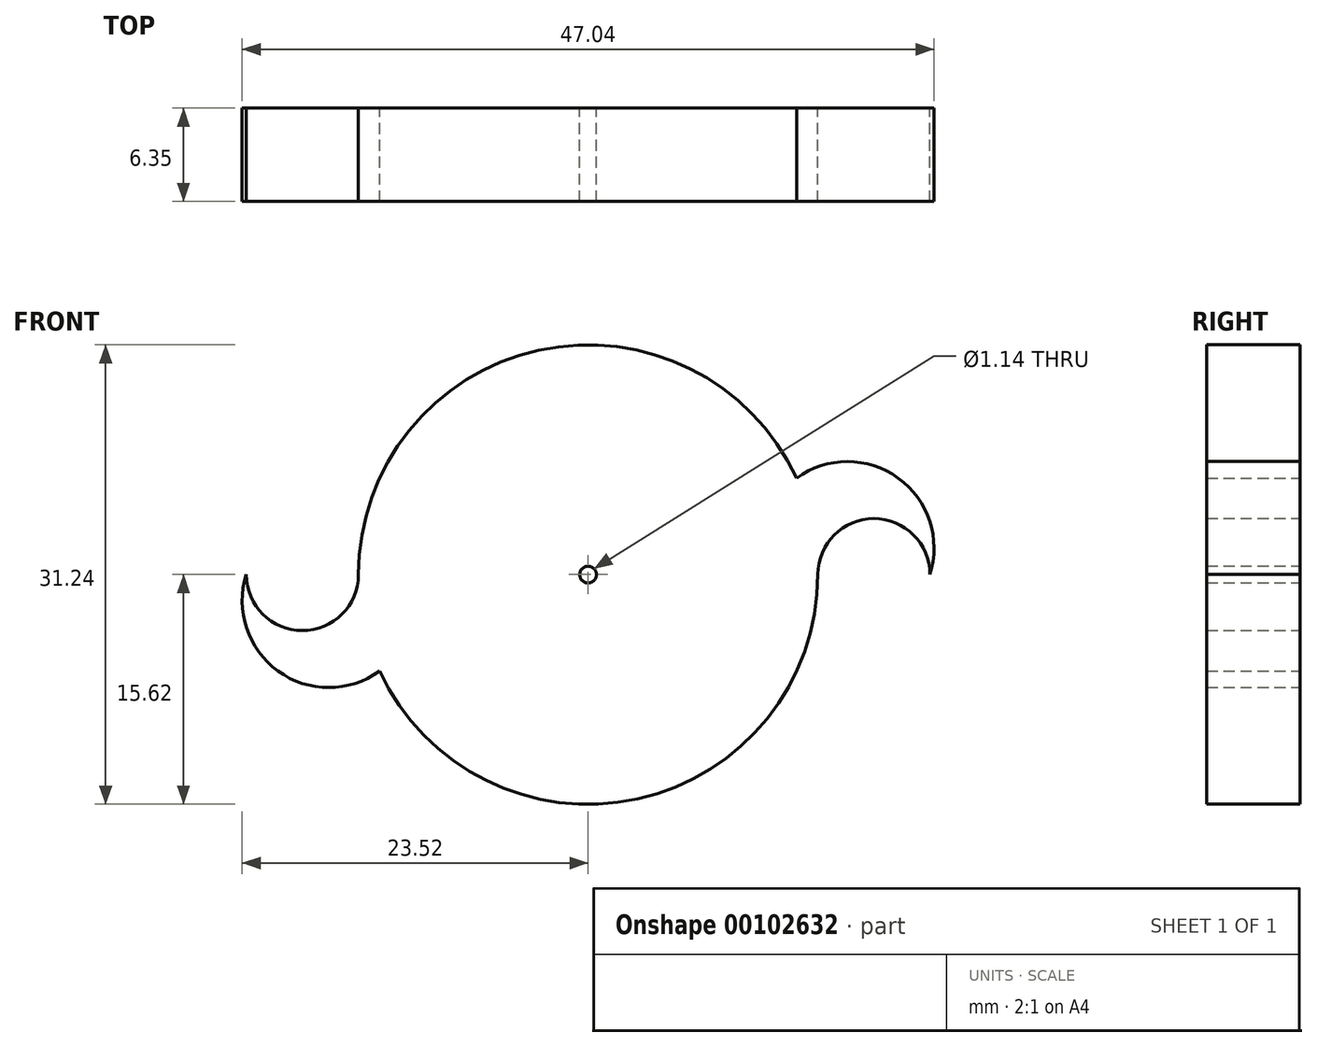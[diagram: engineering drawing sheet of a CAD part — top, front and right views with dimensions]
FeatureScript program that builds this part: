
annotation { "Feature Type Name" : "Feature", "Feature Type Description" : "" }
export const myFeature = defineFeature(function(context is Context, id is Id, definition is map)
    precondition{}
    {
        {
            var Q0;
            Q0=qCreatedBy(makeId("Front.planeOp"),FACE);
            var sketch = newSketch(context, id + "F0", { "sketchPlane" : qUnion([Q0])});
            skArc(sketch, "E0", {"start": v(14.18, 6.56) * mm, "mid": v(-3.36, 15.26) * mm, "end": v(-15.62, 0) * mm});
            skLineSegment(sketch, "E1", {"start": v(31, -8.23) * mm, "end": v(46.62, -8.23) * mm, "construction": true});
            skLineSegment(sketch, "E2", {"start": v(46.62, -8.23) * mm, "end": v(54.24, -8.23) * mm, "construction": true});
            skLineSegment(sketch, "E3", {"start": v(0, 0) * mm, "end": v(15.62, 0) * mm, "construction": true});
            skArc(sketch, "E4", {"start": v(15.62, 0) * mm, "mid": v(19.43, 3.81) * mm, "end": v(23.24, 0) * mm});
            skLineSegment(sketch, "E5", {"start": v(15.62, 0) * mm, "end": v(23.24, 0) * mm, "construction": true});
            skCircle(sketch, "E6", {"center": v(0, 0) * mm, "radius": 0.57 * mm});
            skArc(sketch, "E7", {"start": v(23.24, 0) * mm, "mid": v(21.09, 6.56) * mm, "end": v(14.18, 6.56) * mm});
            skLineSegment(sketch, "E8", {"start": v(17.63, 1.8) * mm, "end": v(19.43, 0) * mm, "construction": true});
            skArc(sketch, "E9.1.0", {"start": v(-23.24, 0) * mm, "mid": v(-21.09, -6.56) * mm, "end": v(-14.18, -6.56) * mm});
            skArc(sketch, "E9.1.1", {"start": v(-15.62, 0) * mm, "mid": v(-19.43, -3.81) * mm, "end": v(-23.24, 0) * mm});
            skArc(sketch, "E10.trimOffspring", {"start": v(-12.14, -9.83) * mm, "mid": v(5.21, -14.73) * mm, "end": v(15.62, 0) * mm});
            skArc(sketch, "E11.trimOffspring", {"start": v(-14.18, -6.56) * mm, "mid": v(-14, -6.92) * mm, "end": v(-13.82, -7.28) * mm});
            skArc(sketch, "E12.trimOffspring", {"start": v(-1.4, -15.56) * mm, "mid": v(10.54, -11.53) * mm, "end": v(15.62, 0) * mm});
            skArc(sketch, "E13.trimOffspring", {"start": v(-14.18, -6.56) * mm, "mid": v(3.36, -15.26) * mm, "end": v(15.62, 0) * mm});
            skSolve(sketch);
        }
        {
            var Q0;
            Q0=qSketchRegion(id+"F0",true);
            extrude(context, id + "F1", {"entities" : qUnion([Q0]), "depth" : 6.35 * mm});
        }
    });
